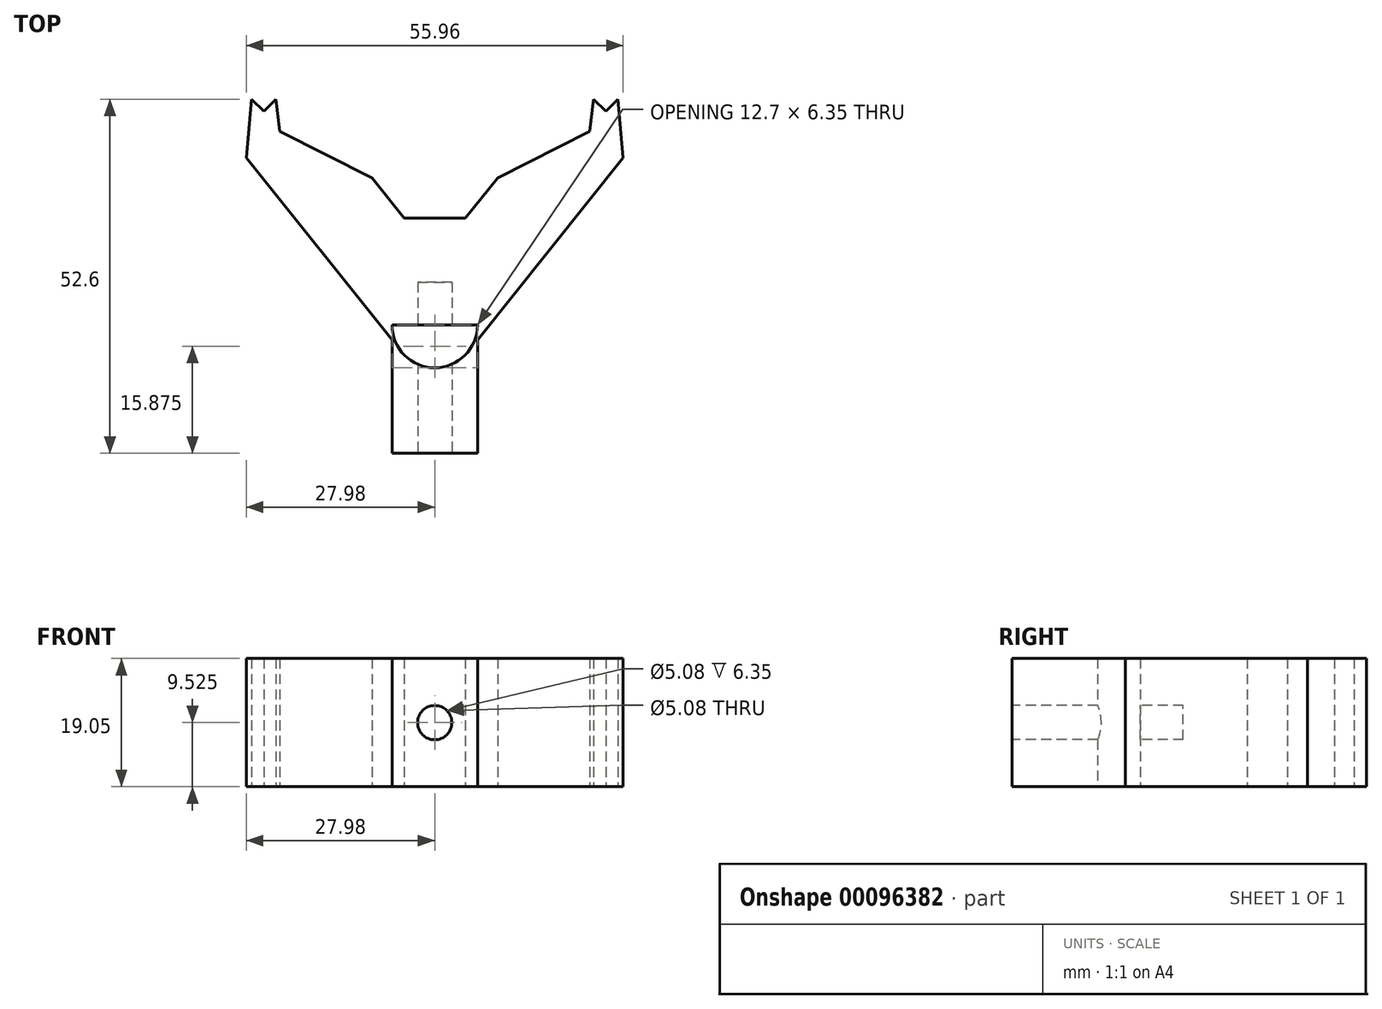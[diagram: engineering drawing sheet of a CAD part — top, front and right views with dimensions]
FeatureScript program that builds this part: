
annotation { "Feature Type Name" : "Feature", "Feature Type Description" : "" }
export const myFeature = defineFeature(function(context is Context, id is Id, definition is map)
    precondition{}
    {
        {
            var Q0;
            Q0=qCreatedBy(makeId("Top.planeOp"),FACE);
            var sketch = newSketch(context, id + "F0", { "sketchPlane" : qUnion([Q0])});
            skLineSegment(sketch, "E0", {"start": v(0, 0) * mm, "end": v(-25.4, 31.75) * mm});
            skLineSegment(sketch, "E1", {"start": v(0, 0) * mm, "end": v(25.4, 31.75) * mm});
            skLineSegment(sketch, "E2", {"start": v(0, 0) * mm, "end": v(0, -19.05) * mm});
            skArc(sketch, "E3.0.startCap", {"start": v(4.96, -3.97) * mm, "mid": v(-3.97, -4.96) * mm, "end": v(-4.96, 3.97) * mm});
            skArc(sketch, "E3.0.endCap", {"start": v(20.44, 35.72) * mm, "mid": v(29.37, 36.7) * mm, "end": v(30.36, 27.78) * mm});
            skLineSegment(sketch, "E3.0.left", {"start": v(-4.96, 3.97) * mm, "end": v(20.44, 35.72) * mm});
            skLineSegment(sketch, "E3.0.right", {"start": v(4.96, -3.97) * mm, "end": v(30.36, 27.78) * mm});
            skArc(sketch, "E4.0.startCap", {"start": v(4.96, 3.97) * mm, "mid": v(3.97, -4.96) * mm, "end": v(-4.96, -3.97) * mm});
            skArc(sketch, "E4.0.endCap", {"start": v(-30.36, 27.78) * mm, "mid": v(-29.37, 36.7) * mm, "end": v(-20.44, 35.72) * mm});
            skLineSegment(sketch, "E4.0.left", {"start": v(-4.96, -3.97) * mm, "end": v(-30.36, 27.78) * mm});
            skLineSegment(sketch, "E4.0.right", {"start": v(4.96, 3.97) * mm, "end": v(-20.44, 35.72) * mm});
            skLineSegment(sketch, "E5", {"start": v(-12.7, 15.88) * mm, "end": v(12.7, 15.88) * mm});
            skLineSegment(sketch, "E6.bottom", {"start": v(6.35, -19.05) * mm, "end": v(-6.35, -19.05) * mm});
            skLineSegment(sketch, "E6.top", {"start": v(6.35, 0) * mm, "end": v(-6.35, 0) * mm});
            skLineSegment(sketch, "E6.left", {"start": v(6.35, -19.05) * mm, "end": v(6.35, 0) * mm});
            skLineSegment(sketch, "E6.right", {"start": v(-6.35, -19.05) * mm, "end": v(-6.35, 0) * mm});
            skPoint(sketch, "E6.middle", {"position": v(0, -9.52) * mm});
            skLineSegment(sketch, "E7", {"start": v(-25.4, 31.75) * mm, "end": v(25.4, 31.75) * mm, "construction": true});
            skLineSegment(sketch, "E8", {"start": v(-25.4, 31.75) * mm, "end": v(-27.2, 33.55) * mm});
            skLineSegment(sketch, "E9", {"start": v(-25.4, 31.75) * mm, "end": v(-23.6, 33.55) * mm});
            skLineSegment(sketch, "E10", {"start": v(-27.2, 33.55) * mm, "end": v(-27.98, 24.8) * mm});
            skLineSegment(sketch, "E11", {"start": v(-23.6, 33.55) * mm, "end": v(-23.02, 28.77) * mm});
            skLineSegment(sketch, "E12", {"start": v(-27.2, 33.55) * mm, "end": v(-23.6, 33.55) * mm, "construction": true});
            skLineSegment(sketch, "E13", {"start": v(25.4, 31.75) * mm, "end": v(23.6, 33.55) * mm});
            skLineSegment(sketch, "E14", {"start": v(25.4, 31.75) * mm, "end": v(27.2, 33.55) * mm});
            skLineSegment(sketch, "E15", {"start": v(23.6, 33.55) * mm, "end": v(23.02, 28.77) * mm});
            skLineSegment(sketch, "E16", {"start": v(27.2, 33.55) * mm, "end": v(27.98, 24.8) * mm});
            skLineSegment(sketch, "E17", {"start": v(23.6, 33.55) * mm, "end": v(27.2, 33.55) * mm, "construction": true});
            skLineSegment(sketch, "E18", {"start": v(23.02, 28.77) * mm, "end": v(9.33, 21.83) * mm});
            skLineSegment(sketch, "E19", {"start": v(-23.02, 28.77) * mm, "end": v(-9.33, 21.83) * mm});
            skSolve(sketch);
        }
        {
            var Q0;
            {var subQ3=sQuery(id+"F0.wireOp",EDGE,"E4.0.startCap");var subQ5=makeQuery(id+"F0.imprint","INTERSECT",VERTEX,{"derivedFrom":[sQuery(id+"F0.wireOp",EDGE,"E3.0.right"),subQ3]});Q0=makeQuery(id+"F0.imprint","IMPRINT",FACE,{"disambiguationData":[TD([[makeQuery(id+"F0.imprint","IMPRINT",EDGE,{"disambiguationData":[TD([[subQ5,-1.0]])],"derivedFrom":subQ3}),-1.0]])]});}
            var Q1;
            {var subQ1=sQuery(id+"F0.wireOp",EDGE,"E2");var subQ3=sQuery(id+"F0.wireOp",EDGE,"E4.0.startCap");var subQ4=makeQuery(id+"F0.imprint","INTERSECT",VERTEX,{"derivedFrom":[subQ1,subQ3]});Q1=makeQuery(id+"F0.imprint","IMPRINT",FACE,{"disambiguationData":[TD([[makeQuery(id+"F0.imprint","IMPRINT",EDGE,{"disambiguationData":[TD([[subQ4,-1.0]])],"derivedFrom":subQ3}),-1.0]])]});}
            var Q2;
            {var subQ3=sQuery(id+"F0.wireOp",EDGE,"E3.0.left");var subQ5=sQuery(id+"F0.wireOp",EDGE,"E3.0.startCap");var subQ6=makeQuery(id+"F0.imprint","INTERSECT",VERTEX,{"derivedFrom":[subQ5,subQ3]});Q2=makeQuery(id+"F0.imprint","IMPRINT",FACE,{"disambiguationData":[TD([[makeQuery(id+"F0.imprint","IMPRINT",EDGE,{"disambiguationData":[TD([[subQ6,-1.0]])],"derivedFrom":subQ3}),-1.0]])]});}
            var Q3;
            {var subQ3=sQuery(id+"F0.wireOp",EDGE,"E4.0.right");var subQ5=sQuery(id+"F0.wireOp",EDGE,"E4.0.startCap");var subQ6=makeQuery(id+"F0.imprint","INTERSECT",VERTEX,{"derivedFrom":[subQ5,subQ3]});Q3=makeQuery(id+"F0.imprint","IMPRINT",FACE,{"disambiguationData":[TD([[makeQuery(id+"F0.imprint","IMPRINT",EDGE,{"disambiguationData":[TD([[subQ6,-1.0]])],"derivedFrom":subQ3}),1.0]])]});}
            var Q4;
            {var subQ1=sQuery(id+"F0.wireOp",EDGE,"E0");var subQ3=sQuery(id+"F0.wireOp",EDGE,"E3.0.left");var subQ4=makeQuery(id+"F0.imprint","INTERSECT",VERTEX,{"derivedFrom":[subQ1,subQ3]});Q4=makeQuery(id+"F0.imprint","IMPRINT",FACE,{"disambiguationData":[TD([[makeQuery(id+"F0.imprint","IMPRINT",EDGE,{"disambiguationData":[TD([[subQ4,-1.0]])],"derivedFrom":subQ3}),-1.0]])]});}
            var Q5;
            {var subQ5=sQuery(id+"F0.wireOp",EDGE,"E8");Q5=makeQuery(id+"F0.imprint","IMPRINT",FACE,{"disambiguationData":[TD([[makeQuery(id+"F0.imprint","IMPRINT",EDGE,{"derivedFrom":subQ5}),1.0]])]});}
            var Q6;
            {var subQ0=sQuery(id+"F0.wireOp",EDGE,"E5");var subQ1=sQuery(id+"F0.wireOp",EDGE,"E0");var subQ2=makeQuery(id+"F0.imprint","INTERSECT",VERTEX,{"derivedFrom":[subQ1,subQ0]});Q6=makeQuery(id+"F0.imprint","IMPRINT",FACE,{"disambiguationData":[TD([[makeQuery(id+"F0.imprint","IMPRINT",EDGE,{"disambiguationData":[TD([[subQ2,1.0]])],"derivedFrom":subQ1}),-1.0]])]});}
            var Q7;
            {var subQ0=sQuery(id+"F0.wireOp",EDGE,"E5");var subQ1=sQuery(id+"F0.wireOp",EDGE,"E1");var subQ2=makeQuery(id+"F0.imprint","INTERSECT",VERTEX,{"derivedFrom":[subQ1,subQ0]});Q7=makeQuery(id+"F0.imprint","IMPRINT",FACE,{"disambiguationData":[TD([[makeQuery(id+"F0.imprint","IMPRINT",EDGE,{"disambiguationData":[TD([[subQ2,1.0]])],"derivedFrom":subQ1}),1.0]])]});}
            var Q8;
            {var subQ0=sQuery(id+"F0.wireOp",EDGE,"E5");var subQ1=sQuery(id+"F0.wireOp",EDGE,"E3.0.left");var subQ2=makeQuery(id+"F0.imprint","INTERSECT",VERTEX,{"derivedFrom":[subQ1,subQ0]});Q8=makeQuery(id+"F0.imprint","IMPRINT",FACE,{"disambiguationData":[TD([[makeQuery(id+"F0.imprint","IMPRINT",EDGE,{"disambiguationData":[TD([[subQ2,1.0]])],"derivedFrom":subQ1}),1.0]])]});}
            var Q9;
            {var subQ4=sQuery(id+"F0.wireOp",EDGE,"E14");Q9=makeQuery(id+"F0.imprint","IMPRINT",FACE,{"disambiguationData":[TD([[makeQuery(id+"F0.imprint","IMPRINT",EDGE,{"derivedFrom":subQ4}),-1.0]])]});}
            var Q10;
            {var subQ3=sQuery(id+"F0.wireOp",EDGE,"E18");Q10=makeQuery(id+"F0.imprint","IMPRINT",FACE,{"disambiguationData":[TD([[makeQuery(id+"F0.imprint","IMPRINT",EDGE,{"derivedFrom":subQ3}),1.0]])]});}
            var Q11;
            {var subQ3=sQuery(id+"F0.wireOp",EDGE,"E19");Q11=makeQuery(id+"F0.imprint","IMPRINT",FACE,{"disambiguationData":[TD([[makeQuery(id+"F0.imprint","IMPRINT",EDGE,{"derivedFrom":subQ3}),-1.0]])]});}
            var Q12;
            {var subQ0=sQuery(id+"F0.wireOp",EDGE,"E13");Q12=makeQuery(id+"F0.imprint","IMPRINT",FACE,{"disambiguationData":[TD([[makeQuery(id+"F0.imprint","IMPRINT",EDGE,{"derivedFrom":subQ0}),1.0]])]});}
            var Q13;
            {var subQ0=sQuery(id+"F0.wireOp",EDGE,"E9");Q13=makeQuery(id+"F0.imprint","IMPRINT",FACE,{"disambiguationData":[TD([[makeQuery(id+"F0.imprint","IMPRINT",EDGE,{"derivedFrom":subQ0}),-1.0]])]});}
            var Q14;
            {var subQ0=sQuery(id+"F0.wireOp",EDGE,"E4.0.left");var subQ3=sQuery(id+"F0.wireOp",EDGE,"E6.right");var subQ5=makeQuery(id+"F0.imprint","INTERSECT",VERTEX,{"derivedFrom":[subQ0,subQ3]});Q14=makeQuery(id+"F0.imprint","IMPRINT",FACE,{"disambiguationData":[TD([[makeQuery(id+"F0.imprint","IMPRINT",EDGE,{"disambiguationData":[TD([[subQ5,1.0]])],"derivedFrom":subQ0}),-1.0]])]});}
            var Q15;
            {var subQ0=sQuery(id+"F0.wireOp",EDGE,"E4.0.startCap");var subQ1=sQuery(id+"F0.wireOp",EDGE,"E3.0.right");var subQ2=makeQuery(id+"F0.imprint","INTERSECT",VERTEX,{"derivedFrom":[subQ1,subQ0]});Q15=makeQuery(id+"F0.imprint","IMPRINT",FACE,{"disambiguationData":[TD([[makeQuery(id+"F0.imprint","IMPRINT",EDGE,{"disambiguationData":[TD([[subQ2,-1.0]])],"derivedFrom":subQ1}),1.0]])]});}
            var Q16;
            {var subQ0=sQuery(id+"F0.wireOp",EDGE,"E6.bottom");var subQ1=sQuery(id+"F0.wireOp",EDGE,"E2");var subQ2=makeQuery(id+"F0.imprint","INTERSECT",VERTEX,{"derivedFrom":[subQ1,subQ0]});Q16=makeQuery(id+"F0.imprint","IMPRINT",FACE,{"disambiguationData":[TD([[makeQuery(id+"F0.imprint","IMPRINT",EDGE,{"disambiguationData":[TD([[subQ2,1.0]])],"derivedFrom":subQ1}),1.0]])]});}
            var Q17;
            {var subQ0=sQuery(id+"F0.wireOp",EDGE,"E6.bottom");var subQ1=sQuery(id+"F0.wireOp",EDGE,"E2");var subQ2=makeQuery(id+"F0.imprint","INTERSECT",VERTEX,{"derivedFrom":[subQ1,subQ0]});Q17=makeQuery(id+"F0.imprint","IMPRINT",FACE,{"disambiguationData":[TD([[makeQuery(id+"F0.imprint","IMPRINT",EDGE,{"disambiguationData":[TD([[subQ2,1.0]])],"derivedFrom":subQ1}),-1.0]])]});}
            extrude(context, id + "F1", {"entities" : qUnion([Q0, Q1, Q2, Q3, Q4, Q5, Q6, Q7, Q8, Q9, Q10, Q11, Q12, Q13, Q14, Q15, Q16, Q17]), "depth" : 19.05 * mm});
        }
        {
            var Q0;
            Q0=makeQuery(id+"F1.opExtrude","SWEPT_FACE",FACE,{"disambiguationData":[OSD([sQuery(id+"F0.wireOp",EDGE,"E6.bottom")])]});
            var sketch = newSketch(context, id + "F2", { "sketchPlane" : qUnion([Q0])});
            skLineSegment(sketch, "E20", {"start": v(-6.35, 19.05) * mm, "end": v(6.35, 0) * mm, "construction": true});
            skLineSegment(sketch, "E21", {"start": v(6.35, 19.05) * mm, "end": v(-6.35, 0) * mm, "construction": true});
            skCircle(sketch, "E22", {"center": v(0, 9.53) * mm, "radius": 2.54 * mm});
            skSolve(sketch);
        }
        {
            var Q0;
            Q0=makeQuery(id+"F2.imprint","IMPRINT",FACE,{"disambiguationData":[TD([[makeQuery(id+"F2.imprint","IMPRINT",EDGE,{"derivedFrom":sQuery(id+"F2.wireOp",EDGE,"E22")}),1.0]])]});
            extrude(context, id + "F3", {"entities" : qUnion([Q0]), "operationType" : NewBodyOperationType.REMOVE, "oppositeDirection" : true, "depth" : 25.4 * mm});
        }
    });
